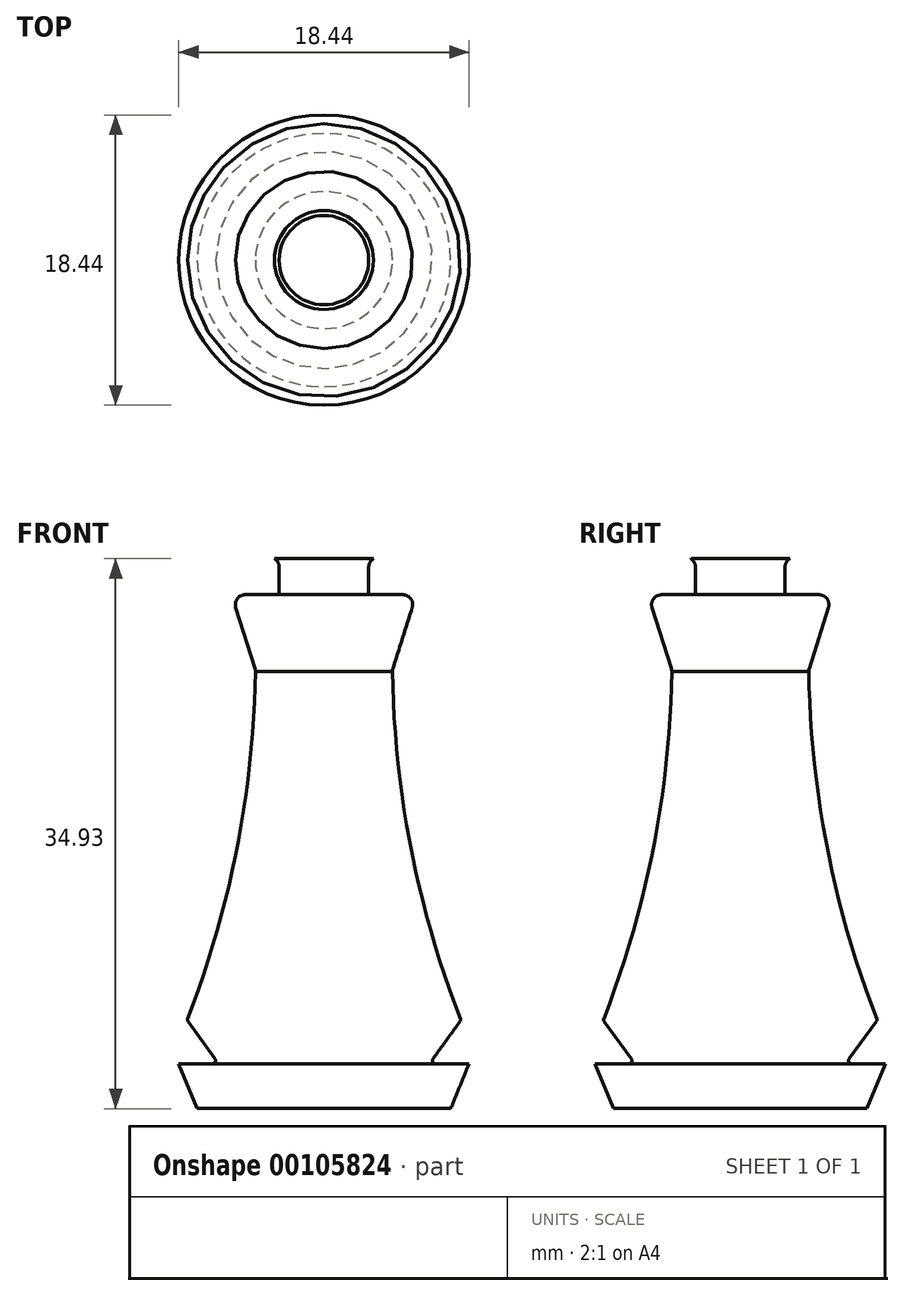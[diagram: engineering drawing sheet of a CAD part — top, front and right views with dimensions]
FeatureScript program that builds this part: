
annotation { "Feature Type Name" : "Feature", "Feature Type Description" : "" }
export const myFeature = defineFeature(function(context is Context, id is Id, definition is map)
    precondition{}
    {
        {
            var Q0;
            Q0=qCreatedBy(makeId("Front.planeOp"),FACE);
            var sketch = newSketch(context, id + "F0", { "sketchPlane" : qUnion([Q0])});
            skLineSegment(sketch, "E0", {"start": v(0, -32.65) * mm, "end": v(8.05, -32.65) * mm});
            skLineSegment(sketch, "E1", {"start": v(8.05, -32.65) * mm, "end": v(9.22, -29.8) * mm});
            skLineSegment(sketch, "E2", {"start": v(9.22, -29.8) * mm, "end": v(6.7, -29.8) * mm});
            skLineSegment(sketch, "E3", {"start": v(6.7, -29.8) * mm, "end": v(8.89, -26.77) * mm});
            skLineSegment(sketch, "E4", {"start": v(8.89, -26.77) * mm, "end": v(4.35, -27.27) * mm});
            skLineSegment(sketch, "E5", {"start": v(4.35, -27.27) * mm, "end": v(4.35, -9.3) * mm});
            skLineSegment(sketch, "E6", {"start": v(4.35, -9.3) * mm, "end": v(4.35, -4.77) * mm});
            skLineSegment(sketch, "E7", {"start": v(4.35, -4.77) * mm, "end": v(5.86, 0) * mm});
            skLineSegment(sketch, "E8", {"start": v(5.86, 0) * mm, "end": v(2.84, 0) * mm});
            skLineSegment(sketch, "E9", {"start": v(2.84, 0) * mm, "end": v(2.84, 2.11) * mm});
            skArc(sketch, "E10", {"start": v(2.84, 2.11) * mm, "mid": v(4.37, 6.48) * mm, "end": v(0, 8) * mm});
            skLineSegment(sketch, "E11", {"start": v(0, 8) * mm, "end": v(0, -32.65) * mm});
            skSolve(sketch);
        }
        {
            var Q0;
            Q0=makeQuery(id+"F0.imprint","IMPRINT",FACE,{"disambiguationData":[TD([[makeQuery(id+"F0.imprint","IMPRINT",EDGE,{"derivedFrom":sQuery(id+"F0.wireOp",EDGE,"E0")}),1.0]])]});
            var Q1;
            Q1=sQuery(id+"F0.wireOp",EDGE,"E11");
            revolve(context, id + "F1", {"entities" : qUnion([Q0]), "axis" : qUnion([Q1]), "revolveType" : RevolveType.FULL});
        }
        {
            var Q0;
            Q0=makeQuery(id+"F1.opRevolve","SWEPT_FACE",FACE,{"disambiguationData":[OSD([sQuery(id+"F0.wireOp",EDGE,"E7")])]});
            var Q1;
            Q1=makeQuery(id+"F1.opRevolve","SWEPT_EDGE",EDGE,{"disambiguationData":[OSD([sQuery(id+"F0.wireOp",EDGE,"E6"),sQuery(id+"F0.wireOp",EDGE,"E7")])]});
            var Q2;
            Q2=makeQuery(id+"F1.opRevolve","SWEPT_EDGE",EDGE,{"disambiguationData":[OSD([sQuery(id+"F0.wireOp",EDGE,"E9"),sQuery(id+"F0.wireOp",EDGE,"E10")])]});
            fillet(context, id + "F2", {"entities" : qUnion([Q0, Q1, Q2]), "radius" : 0.64 * mm, "tangentPropagation" : true, "allowEdgeOverflow" : false});
        }
        {
            var Q0;
            Q0=makeQuery(id+"F1.opRevolve","SWEPT_EDGE",EDGE,{"disambiguationData":[OSD([sQuery(id+"F0.wireOp",EDGE,"E3"),sQuery(id+"F0.wireOp",EDGE,"E4")])]});
            var Q1;
            Q1=makeQuery(id+"F1.opRevolve","SWEPT_FACE",FACE,{"disambiguationData":[OSD([sQuery(id+"F0.wireOp",EDGE,"E3")])]});
            fillet(context, id + "F3", {"entities" : qUnion([Q0, Q1]), "radius" : 0.18 * mm, "tangentPropagation" : true, "allowEdgeOverflow" : false});
        }
        {
            var Q0;
            Q0=makeQuery(id+"F1.opRevolve","SWEPT_EDGE",EDGE,{"disambiguationData":[OSD([sQuery(id+"F0.wireOp",EDGE,"E4"),sQuery(id+"F0.wireOp",EDGE,"E5")])]});
            fillet(context, id + "F4", {"entities" : qUnion([Q0]), "radius" : 63.5 * mm, "tangentPropagation" : true, "allowEdgeOverflow" : false});
        }
    });
